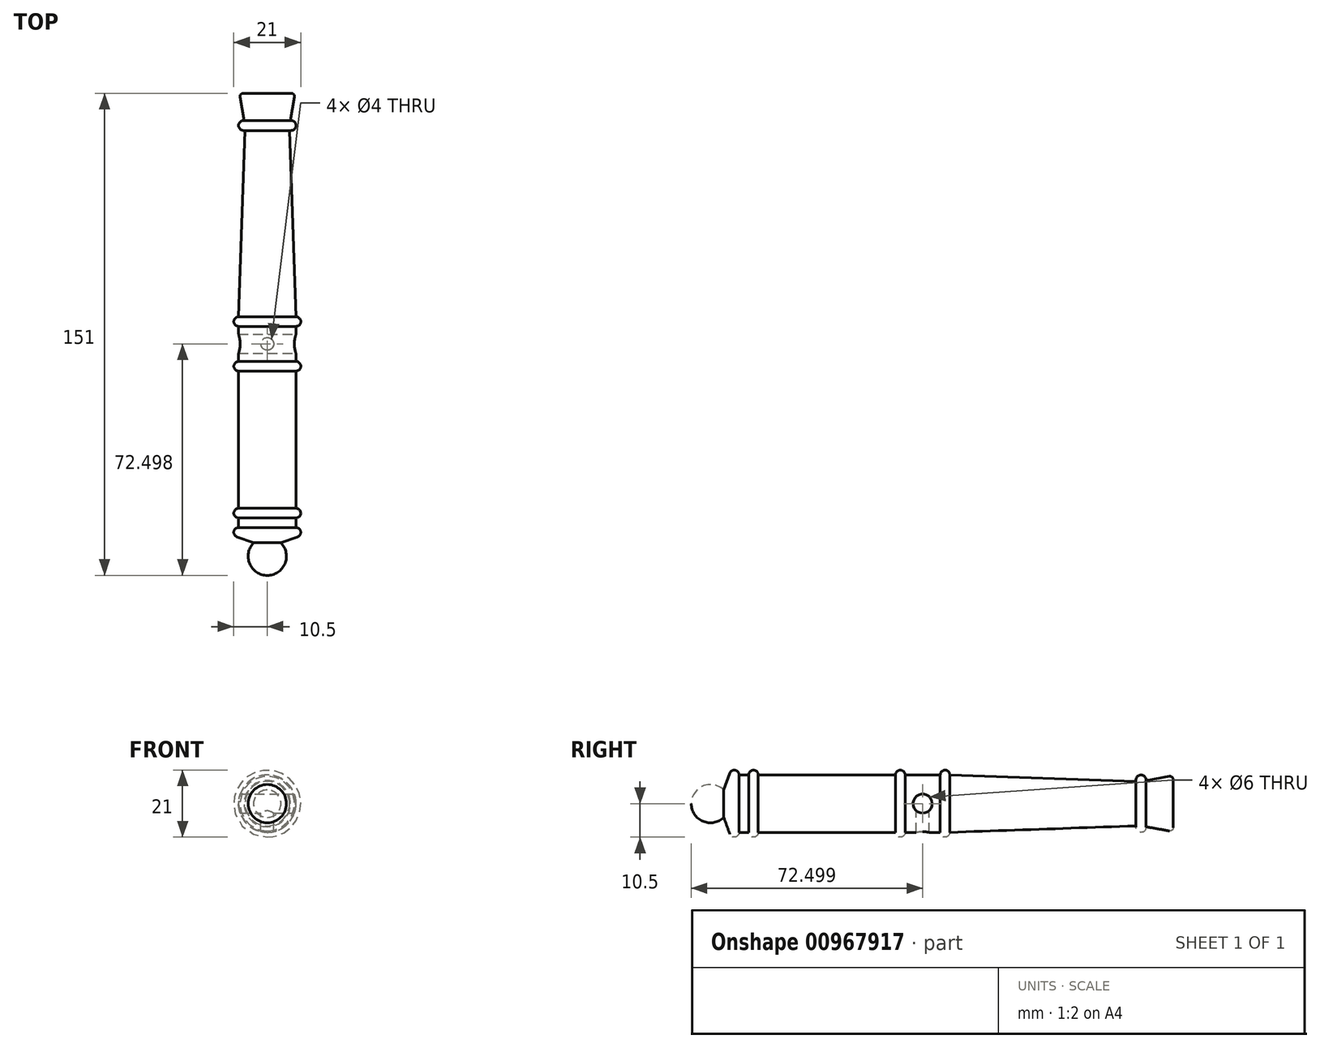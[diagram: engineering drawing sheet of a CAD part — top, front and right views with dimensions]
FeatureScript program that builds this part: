
annotation { "Feature Type Name" : "Feature", "Feature Type Description" : "" }
export const myFeature = defineFeature(function(context is Context, id is Id, definition is map)
    precondition{}
    {
        {
            var Q0;
            Q0=qCreatedBy(makeId("Right.planeOp"),FACE);
            var sketch = newSketch(context, id + "F0", { "sketchPlane" : qUnion([Q0])});
            skLineSegment(sketch, "E0.bottom", {"start": v(-4.56, 9) * mm, "end": v(-1.56, 9) * mm});
            skPoint(sketch, "E0.middle", {"position": v(0, 0) * mm});
            skPoint(sketch, "E1.midSnap0", {"position": v(3.47, 9) * mm});
            skPoint(sketch, "E1.midSnap1", {"position": v(-10.03, 13.53) * mm});
            skLineSegment(sketch, "E2", {"start": v(0, 0) * mm, "end": v(59.78, 0) * mm});
            skLineSegment(sketch, "E3", {"start": v(59.78, 7.25) * mm, "end": v(59.78, 7.41) * mm});
            skLineSegment(sketch, "E4", {"start": v(62.78, 0) * mm, "end": v(59.78, 0) * mm});
            skLineSegment(sketch, "E5", {"start": v(71.44, 7.56) * mm, "end": v(71.44, 0) * mm});
            skLineSegment(sketch, "E6", {"start": v(70.26, 8.54) * mm, "end": v(62.94, 7.25) * mm});
            skLineSegment(sketch, "E7", {"start": v(71.44, 0) * mm, "end": v(62.78, 0) * mm});
            skPoint(sketch, "E8.visualSharp", {"position": v(71.44, 8.75) * mm});
            skArc(sketch, "E8.filletArc", {"start": v(71.44, 7.56) * mm, "mid": v(71.08, 8.32) * mm, "end": v(70.26, 8.54) * mm});
            skArc(sketch, "E9", {"start": v(62.94, 7.25) * mm, "mid": v(61.44, 9) * mm, "end": v(59.78, 7.41) * mm});
            skLineSegment(sketch, "E10", {"start": v(-15.56, 9) * mm, "end": v(-58.56, 9) * mm});
            skLineSegment(sketch, "E11", {"start": v(-60.9, 0) * mm, "end": v(0, 0) * mm});
            skLineSegment(sketch, "E12", {"start": v(-63.9, 0) * mm, "end": v(-60.9, 0) * mm});
            skLineSegment(sketch, "E13", {"start": v(-61.56, 9) * mm, "end": v(-64.56, 9) * mm});
            skLineSegment(sketch, "E14", {"start": v(-66.9, 0) * mm, "end": v(-63.9, 0) * mm});
            skArc(sketch, "E15", {"start": v(-58.56, 9) * mm, "mid": v(-60.06, 10.5) * mm, "end": v(-61.56, 9) * mm});
            skLineSegment(sketch, "E16", {"start": v(-71.7, 0) * mm, "end": v(-66.9, 0) * mm});
            skArc(sketch, "E17", {"start": v(-69.37, 4.3) * mm, "mid": v(-75.9, 5.53) * mm, "end": v(-79.56, 0) * mm});
            skArc(sketch, "E18", {"start": v(-64.56, 9) * mm, "mid": v(-66.06, 10.5) * mm, "end": v(-67.56, 9) * mm});
            skLineSegment(sketch, "E19", {"start": v(-69.37, 4.3) * mm, "end": v(-67.47, 9.51) * mm});
            skPoint(sketch, "E20.orphan", {"position": v(-72.4, 0) * mm});
            skPoint(sketch, "E0.top.end.orphan", {"position": v(4.56, -9) * mm});
            skPoint(sketch, "E21.start.orphan", {"position": v(-5.5, -9) * mm});
            skLineSegment(sketch, "E22", {"start": v(-79.56, 0) * mm, "end": v(-71.7, 0) * mm});
            skPoint(sketch, "E1.end.orphan", {"position": v(5.5, 9) * mm});
            skLineSegment(sketch, "E23", {"start": v(-4.56, 9) * mm, "end": v(-12.56, 9) * mm});
            skLineSegment(sketch, "E24", {"start": v(1.44, 0) * mm, "end": v(-1.56, 0) * mm});
            skPoint(sketch, "E24.endSnap0", {"position": v(-1.56, 9) * mm});
            skLineSegment(sketch, "E25", {"start": v(-12.56, 0) * mm, "end": v(-15.56, 0) * mm});
            skArc(sketch, "E26", {"start": v(-12.56, 9) * mm, "mid": v(-14.06, 10.5) * mm, "end": v(-15.56, 9) * mm});
            skArc(sketch, "E27", {"start": v(1.44, 9) * mm, "mid": v(-0.06, 10.5) * mm, "end": v(-1.56, 9) * mm});
            skLineSegment(sketch, "E28", {"start": v(59.78, 6.96) * mm, "end": v(59.78, 7.25) * mm});
            skLineSegment(sketch, "E29", {"start": v(1.44, 9) * mm, "end": v(58.65, 7) * mm});
            skLineSegment(sketch, "E30", {"start": v(58.65, 7) * mm, "end": v(59.78, 6.96) * mm});
            skLineSegment(sketch, "E31", {"start": v(-12.56, 0) * mm, "end": v(-7.06, 0) * mm});
            skSolve(sketch);
        }
        {
            var Q0;
            Q0=makeQuery(id+"F0.imprint","IMPRINT",FACE,{"disambiguationData":[TD([[makeQuery(id+"F0.imprint","IMPRINT",EDGE,{"derivedFrom":sQuery(id+"F0.wireOp",EDGE,"E0.bottom")}),-1.0]])]});
            var Q1;
            {var subQ0=sQuery(id+"F0.wireOp",EDGE,"E31");var subQ1=sQuery(id+"F0.wireOp",EDGE,"E11");var subQ2=makeQuery(id+"F0.imprint","INTERSECT",VERTEX,{"derivedFrom":[subQ1,subQ0]});Q1=makeQuery(id+"F0.imprint","IMPRINT",FACE,{"disambiguationData":[TD([[makeQuery(id+"F0.imprint","IMPRINT",EDGE,{"disambiguationData":[TD([[subQ2,-1.0]])],"derivedFrom":subQ1}),1.0]])]});}
            var Q2;
            Q2=sQuery(id+"F0.wireOp",EDGE,"E2");
            revolve(context, id + "F1", {"surfaceOperationType" : NewSurfaceOperationType.NEW, "entities" : qUnion([Q0, Q1]), "axis" : qUnion([Q2]), "revolveType" : RevolveType.FULL});
        }
        {
            var Q0;
            Q0=qCreatedBy(makeId("Right.planeOp"),FACE);
            var sketch = newSketch(context, id + "F2", { "sketchPlane" : qUnion([Q0])});
            skCircle(sketch, "E32", {"center": v(-7.06, 0) * mm, "radius": 3 * mm});
            skSolve(sketch);
        }
        {
            var Q0;
            Q0 = qSketchRegion(id + "F2", true);
            extrude(context, id + "F3", {"entities" : qUnion([Q0]), "operationType" : NewBodyOperationType.REMOVE, "oppositeDirection" : true, "depth" : 50 * mm, "offsetDistance" : 25 * mm, "symmetric" : true});
        }
        {
            var Q0;
            Q0=qCreatedBy(makeId("Top.planeOp"),FACE);
            var sketch = newSketch(context, id + "F4", { "sketchPlane" : qUnion([Q0])});
            skCircle(sketch, "E33", {"center": v(0, -7.06) * mm, "radius": 2 * mm});
            skSolve(sketch);
        }
        {
            var Q0;
            Q0 = qSketchRegion(id + "F4", true);
            extrude(context, id + "F5", {"entities" : qUnion([Q0]), "operationType" : NewBodyOperationType.REMOVE, "oppositeDirection" : true, "depth" : 25 * mm, "offsetDistance" : 25 * mm});
        }
    });
